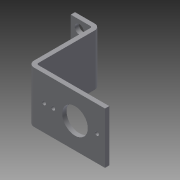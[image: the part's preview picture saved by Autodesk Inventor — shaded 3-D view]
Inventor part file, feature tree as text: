
AUTODESK INVENTOR PART (.ipt)
format: ipt  version: 2013 (Build 170138000, 138)  size: 225,280 bytes
history: native  units: in
note: dims shown in document units (in); Inventor stores cm internally (conversion verified against a paired STEP export)
features: sheet_metal_op x7, other x7, sketch x6, reference x4
ambient origin geometry x8: Origin, YZ Plane, XZ Plane, XY Plane, X Axis, Y Axis, Z Axis, Center Point
bodies: Solid1 (feature_tree)
feature tree (24):
  sheet_metal_op  "Face1"
  sheet_metal_op  "Flange1"
  sheet_metal_op  "Flange2"
  sketch  "Sketch1"  dims[d0=1.5in]
  other  "Plate1"
  sketch  "Sketch2"  dims[d1=0.75in]
  other  "Plate2"
  sheet_metal_op  "Bend1"
  sheet_metal_op  "Corner1"
  sketch  "Sketch3"  dims[d2=0.266in]
  other  "Plate3"
  sheet_metal_op  "Bend2"
  sheet_metal_op  "Corner2"
  sketch  "Sketch4"  dims[d3=0.266in]
  reference  "Reference1"
  sketch  "Sketch5"  dims[d4=1.0in]
  reference  "Reference2"
  reference  "Reference3"
  reference  "Reference4"
  sketch  "Sketch6"  dims[d5=0.25in d6=0.25in d7=0.25in d8=0.125in d9=0.125in d10=0.0625in d11=0.25in d12=0.125in d13=2.0in d14=90.0deg d15=0.05in d16=0.5in d17=0.125in d18=0.125in d19=0.125in d20=0.0625in d21=0.25in d22=0.125in d23=2.25in d24=90.0deg d25=0.05in d26=0.5in d27=0.125in d28=0.125in d29=0.5in d31=0.125in d32=0.0in d33=0.125in d34=0.0in d35=0.748in d36=0.125in d37=0.0in]
  other  "Cut1"
  other  "Cut2"
  other  "Cut3"
  other  "Definition1"
